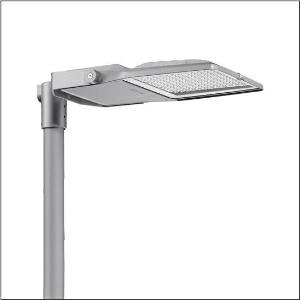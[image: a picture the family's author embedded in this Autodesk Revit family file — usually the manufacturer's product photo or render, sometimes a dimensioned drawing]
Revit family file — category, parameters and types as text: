
# Revit family: floodlight_fl_21_midi___pl33t_5xa7785e2f3a_9b27
name_source: partatom
category: Lighting Fixtures
units: mm (PartAtom-declared; Revit-internal decimal feet)

## family parameters
Cut with Voids When Loaded = No
Host = Face
Light Source = No
Part Type = Normal
Room Calculation Point = No
Round Connector Dimension = Use Diameter
Shared = No

## types (1)
- --- (1 x LED, 26630 lm, 212.4 W, 3000K)
    Apparent Load = 212 VA
    CIE Flux Codes = 26 75 99 100 100
    Color Rendering = 70
    Color Temperature = 3000K
    Default Elevation = 1800 mm
    Description = Floodlight FL 21 midi, floodlight, primary light control with lens, of PMMA, primary optical cover: protective disc, of toughened safety glass, transparent, light distribution: PL33T, light emission: direct distribution, installation type: surface-mounted, LED, High Power LED, rated luminous flux: 26.630lm, luminous efficacy: 125lm/W, light colour: 730, colour temperature: 3000K, control gear: ECG Smart Interface, control: flexible luminous flux parameterisation, time-dependent luminous flux control, constant luminous flux control, overheat protection, presetting dimming logarithmic, with terminal, 6-pole, mains connection: 220..240V, AC, 50/60Hz, start of lifetime: 212W, end of service life: 231W, reduction: 95W, luminaire housing, of diecast aluminium, powder-coated, Siteco® metallic grey (DB 702S), sealing non-destructively replaceable, please order mast flange separately, mast bracket, of steel, galvanised, powder-coated, Siteco® metallic grey (DB 702S), Smart Interface above, protection rating (complete): IP66, insulation class (complete): insulation class II (safety insulation), certification: CE, protection symbol: D, impact resistance: IK08, permissible operating ambient temperature: -20..+40°C, permissible operating ambient temperature for outdoor applications: -40..+50°C, standard: DIN EN 12944, LABS conformity tested according to VDMA 24364:2018-05, packaging unit: 1 piece

Light Distribution: PL33T
    Height = 76 mm
    Lamp = 1 x LED
    Lamp Light Flux = 26630 lm
    Lamp Power = 212.4 W
    Lamp count = 1
    Length = 657 mm
    Luminous efficacy = 125 lm/W
    Manufacturer = Siteco
    ModVariant = No
    Model = 5XA7785E2F3A
    Number of Poles = 1
    OnlyDefault = Yes
    Power Factor = 1
    Product Name = Floodlight FL 21 midi | PL33T
    Product group = floodlight | pylon annexe
    ProductGroupID = 6200
    Protection Class = Protection class II
    Protection Degree = IP 66
    RLX_Detail_Level = 1
    RLX_Emergency_Light_Flux = 0 lm
    RLX_Emergency_Type = 0
    RLX_Emergency_Type_DB = No
    RlxData = <blob elided: 153185 chars, md5=1cd899b3>
    Socket = socket
    Standby Power = 0 W
    System Light Flux = 26630 lm
    System Power = 212 W
    Type Comments = factory setting: luminous flux: 100 % | dim-lin: 254 | 710 mA
    Type Image = l_1007123.jpg
    URL = http://relux.com
    VarID = @adj_100777
    Voltage = 0 V
    Weight = 0.00 kg
    Width = 442 mm

## geometry (parser evidence)
native form markers: Blend x4, Sweep x12
no freeform markers — native parametric forms only
